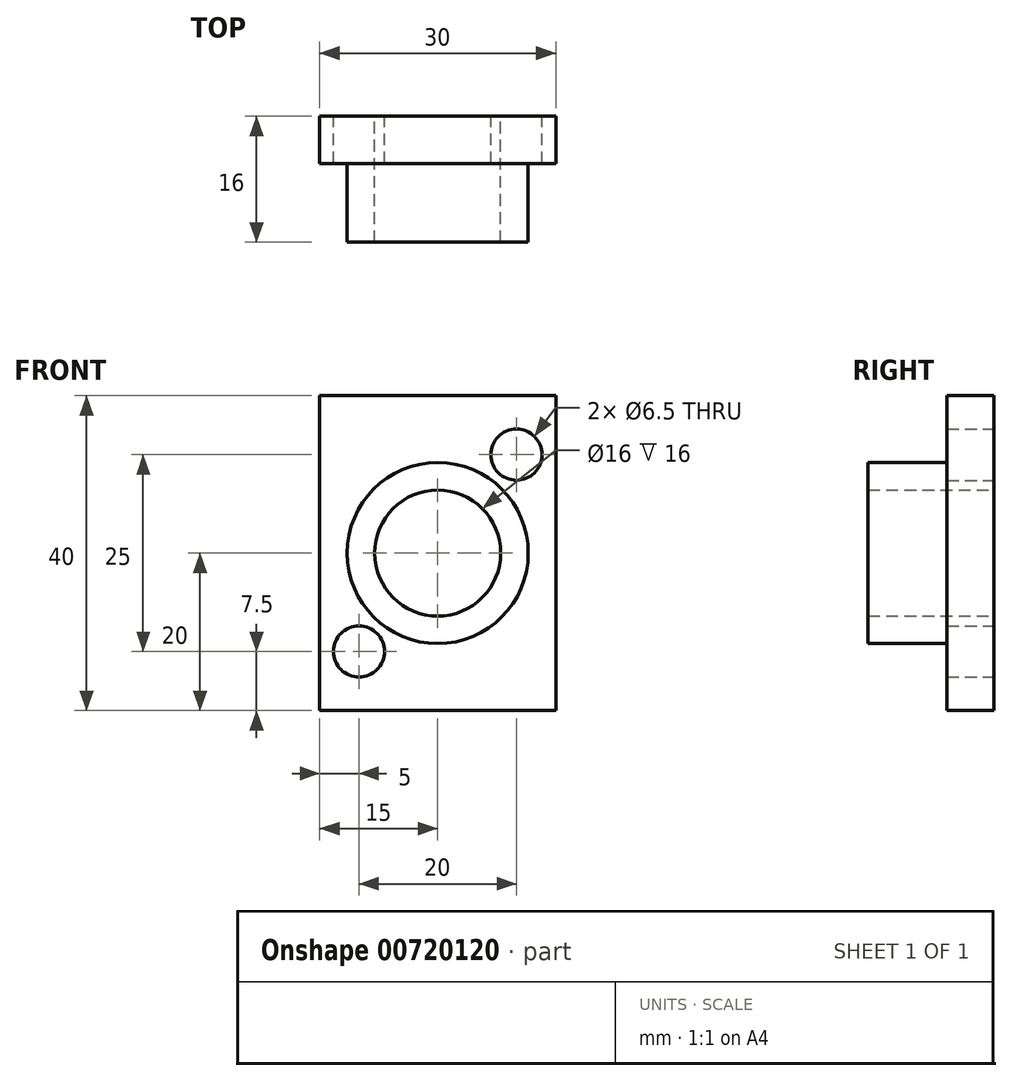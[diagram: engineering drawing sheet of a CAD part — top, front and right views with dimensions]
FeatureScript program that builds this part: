
annotation { "Feature Type Name" : "Feature", "Feature Type Description" : "" }
export const myFeature = defineFeature(function(context is Context, id is Id, definition is map)
    precondition{}
    {
        {
            var Q0;
            Q0=qCreatedBy(makeId("Front.planeOp"),FACE);
            var sketch = newSketch(context, id + "F0", { "sketchPlane" : qUnion([Q0])});
            skLineSegment(sketch, "E0.bottom", {"start": v(0, 0) * mm, "end": v(30, 0) * mm});
            skLineSegment(sketch, "E0.top", {"start": v(0, 40) * mm, "end": v(30, 40) * mm});
            skLineSegment(sketch, "E0.left", {"start": v(0, 0) * mm, "end": v(0, 40) * mm});
            skLineSegment(sketch, "E0.right", {"start": v(30, 0) * mm, "end": v(30, 40) * mm});
            skCircle(sketch, "E1", {"center": v(15, 20) * mm, "radius": 8 * mm});
            skPoint(sketch, "E1.centerSnap0", {"position": v(15, 40) * mm});
            skPoint(sketch, "E1.centerSnap1", {"position": v(0, 20) * mm});
            skCircle(sketch, "E2", {"center": v(25, 32.5) * mm, "radius": 3.25 * mm});
            skCircle(sketch, "E3", {"center": v(5, 7.5) * mm, "radius": 3.25 * mm});
            skSolve(sketch);
        }
        {
            var Q0;
            Q0=makeQuery(id+"F0.imprint","IMPRINT",FACE,{"disambiguationData":[TD([[makeQuery(id+"F0.imprint","IMPRINT",EDGE,{"derivedFrom":sQuery(id+"F0.wireOp",EDGE,"E0.bottom")}),1.0]])]});
            extrude(context, id + "F1", {"entities" : qUnion([Q0]), "depth" : 6 * mm, "offsetDistance" : 25 * mm});
        }
        {
            var Q0;
            Q0=makeQuery(id+"F1.opExtrude","CAP_FACE",FACE,{"disambiguationData":[OSD([sQuery(id+"F0.wireOp",EDGE,"E0.bottom"),sQuery(id+"F0.wireOp",EDGE,"E0.top"),sQuery(id+"F0.wireOp",EDGE,"E0.left"),sQuery(id+"F0.wireOp",EDGE,"E0.right"),sQuery(id+"F0.wireOp",EDGE,"E1"),sQuery(id+"F0.wireOp",EDGE,"E2"),sQuery(id+"F0.wireOp",EDGE,"E3")])],"isStart":false});
            var sketch = newSketch(context, id + "F2", { "sketchPlane" : qUnion([Q0])});
            skCircle(sketch, "E4", {"center": v(15, 20) * mm, "radius": 11.5 * mm});
            skSolve(sketch);
        }
        {
            var Q0;
            Q0=makeQuery(id+"F2.imprint","IMPRINT",FACE,{"disambiguationData":[TD([[makeQuery(id+"F2.imprint","IMPRINT",EDGE,{"derivedFrom":sQuery(id+"F2.wireOp",EDGE,"E4")}),1.0]])]});
            extrude(context, id + "F3", {"entities" : qUnion([Q0]), "operationType" : NewBodyOperationType.ADD, "depth" : 10 * mm, "offsetDistance" : 25 * mm});
        }
    });
